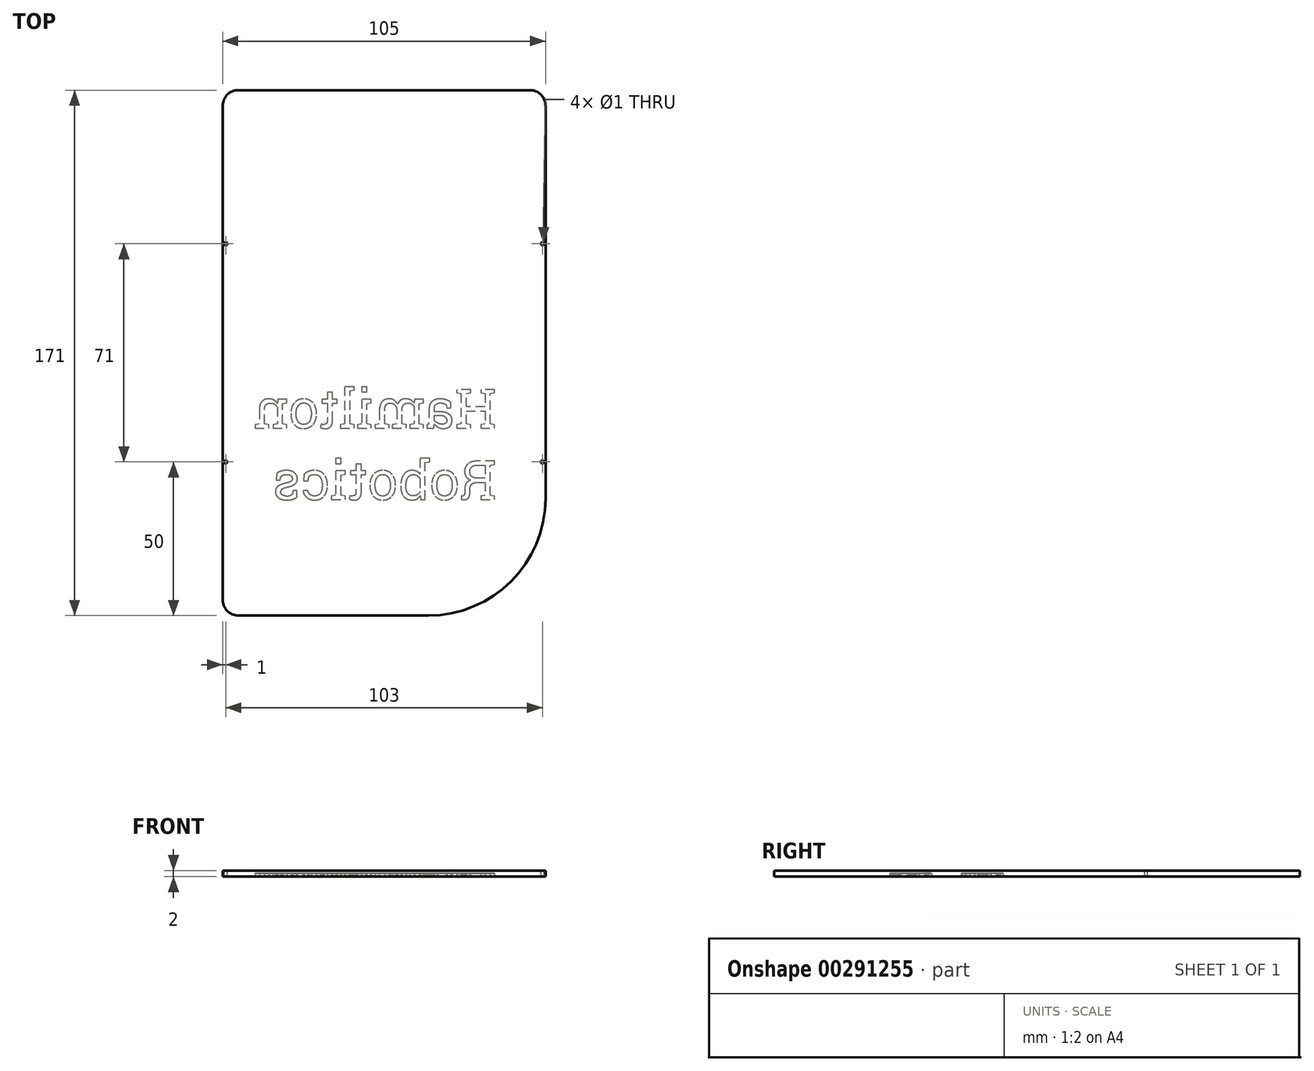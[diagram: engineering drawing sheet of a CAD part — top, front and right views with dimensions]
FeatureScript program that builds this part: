
annotation { "Feature Type Name" : "Feature", "Feature Type Description" : "" }
export const myFeature = defineFeature(function(context is Context, id is Id, definition is map)
    precondition{}
    {
        {
            var Q0;
            Q0=qCreatedBy(makeId("Top.planeOp"),FACE);
            var sketch = newSketch(context, id + "F0", { "sketchPlane" : qUnion([Q0])});
            skLineSegment(sketch, "E0.bottom", {"start": v(0, 0) * mm, "end": v(105, 0) * mm});
            skLineSegment(sketch, "E0.top", {"start": v(0, 171) * mm, "end": v(105, 171) * mm});
            skLineSegment(sketch, "E0.left", {"start": v(0, 0) * mm, "end": v(0, 171) * mm});
            skLineSegment(sketch, "E0.right", {"start": v(105, 0) * mm, "end": v(105, 171) * mm});
            skSolve(sketch);
        }
        {
            var Q0;
            Q0=makeQuery(id+"F0.imprint","IMPRINT",FACE,{"disambiguationData":[TD([[makeQuery(id+"F0.imprint","IMPRINT",EDGE,{"derivedFrom":sQuery(id+"F0.wireOp",EDGE,"E0.bottom")}),1.0]])]});
            extrude(context, id + "F1", {"entities" : qUnion([Q0]), "depth" : 2 * mm});
        }
        {
            var Q0;
            Q0=makeQuery(id+"F1.opExtrude","SWEPT_EDGE",EDGE,{"disambiguationData":[OSD([sQuery(id+"F0.wireOp",EDGE,"E0.bottom"),sQuery(id+"F0.wireOp",EDGE,"E0.left")])]});
            var Q1;
            Q1=makeQuery(id+"F1.opExtrude","SWEPT_EDGE",EDGE,{"disambiguationData":[OSD([sQuery(id+"F0.wireOp",EDGE,"E0.top"),sQuery(id+"F0.wireOp",EDGE,"E0.left")])]});
            var Q2;
            Q2=makeQuery(id+"F1.opExtrude","SWEPT_EDGE",EDGE,{"disambiguationData":[OSD([sQuery(id+"F0.wireOp",EDGE,"E0.top"),sQuery(id+"F0.wireOp",EDGE,"E0.right")])]});
            fillet(context, id + "F2", {"entities" : qUnion([Q0, Q1, Q2]), "radius" : 5.08 * mm, "tangentPropagation" : true, "allowEdgeOverflow" : false});
        }
        {
            var Q0;
            Q0=makeQuery(id+"F1.opExtrude","SWEPT_EDGE",EDGE,{"disambiguationData":[OSD([sQuery(id+"F0.wireOp",EDGE,"E0.bottom"),sQuery(id+"F0.wireOp",EDGE,"E0.right")])]});
            fillet(context, id + "F3", {"entities" : qUnion([Q0]), "radius" : 38.1 * mm, "tangentPropagation" : true, "allowEdgeOverflow" : false});
        }
        {
            var Q0;
            Q0=makeQuery(id+"F1.opExtrude","CAP_FACE",FACE,{"disambiguationData":[OSD([sQuery(id+"F0.wireOp",EDGE,"E0.bottom"),sQuery(id+"F0.wireOp",EDGE,"E0.top"),sQuery(id+"F0.wireOp",EDGE,"E0.left"),sQuery(id+"F0.wireOp",EDGE,"E0.right")])],"isStart":true});
            var sketch = newSketch(context, id + "F4", { "sketchPlane" : qUnion([Q0])});
            skText(sketch, "E1", { "text": "Hamilton\nRobotics", "fontName": "RobotoSlab-Regular.ttf"});
            const initialGuessF4  = {"E1": [0.08904, -0.06103, -1, 0, 0.0127]};
            skSetInitialGuess(sketch, initialGuessF4);
            skSolve(sketch);
        }
        {
            var Q0;
            Q0 = qSketchRegion(id + "F4", true);
            extrude(context, id + "F5", {"entities" : qUnion([Q0]), "operationType" : NewBodyOperationType.REMOVE, "oppositeDirection" : true, "depth" : 1 * mm});
        }
        {
            var Q0;
            Q0=makeQuery(id+"F1.opExtrude","CAP_FACE",FACE,{"disambiguationData":[OSD([sQuery(id+"F0.wireOp",EDGE,"E0.bottom"),sQuery(id+"F0.wireOp",EDGE,"E0.top"),sQuery(id+"F0.wireOp",EDGE,"E0.left"),sQuery(id+"F0.wireOp",EDGE,"E0.right")])],"isStart":false});
            var sketch = newSketch(context, id + "F6", { "sketchPlane" : qUnion([Q0])});
            skLineSegment(sketch, "E2.bottom", {"start": v(0, 171) * mm, "end": v(105, 171) * mm, "construction": true});
            skLineSegment(sketch, "E2.top", {"start": v(0, 0) * mm, "end": v(105, 0) * mm, "construction": true});
            skLineSegment(sketch, "E2.left", {"start": v(0, 171) * mm, "end": v(0, 0) * mm, "construction": true});
            skLineSegment(sketch, "E2.right", {"start": v(105, 171) * mm, "end": v(105, 0) * mm, "construction": true});
            skLineSegment(sketch, "E3", {"start": v(1, 171) * mm, "end": v(1, 121) * mm, "construction": true});
            skLineSegment(sketch, "E4", {"start": v(104, 171) * mm, "end": v(104, 121) * mm, "construction": true});
            skLineSegment(sketch, "E5", {"start": v(1, 0) * mm, "end": v(1, 50) * mm, "construction": true});
            skLineSegment(sketch, "E6", {"start": v(104, 0) * mm, "end": v(104, 50) * mm, "construction": true});
            skLineSegment(sketch, "E7", {"start": v(0, 144.65) * mm, "end": v(1, 144.65) * mm, "construction": true});
            skLineSegment(sketch, "E8", {"start": v(105, 150) * mm, "end": v(104, 150) * mm, "construction": true});
            skLineSegment(sketch, "E9", {"start": v(0, 18.36) * mm, "end": v(1, 18.36) * mm, "construction": true});
            skLineSegment(sketch, "E10", {"start": v(105, 18.16) * mm, "end": v(104, 18.16) * mm, "construction": true});
            skCircle(sketch, "E11", {"center": v(1, 50) * mm, "radius": 0.5 * mm});
            skCircle(sketch, "E12", {"center": v(104, 50) * mm, "radius": 0.5 * mm});
            skCircle(sketch, "E13", {"center": v(104, 121) * mm, "radius": 0.5 * mm});
            skCircle(sketch, "E14", {"center": v(1, 121) * mm, "radius": 0.5 * mm});
            skSolve(sketch);
        }
        {
            var Q0;
            Q0 = qSketchRegion(id + "F6", true);
            extrude(context, id + "F7", {"entities" : qUnion([Q0]), "operationType" : NewBodyOperationType.REMOVE, "endBound" : BoundingType.THROUGH_ALL, "oppositeDirection" : true, "depth" : 25.4 * mm});
        }
    });
